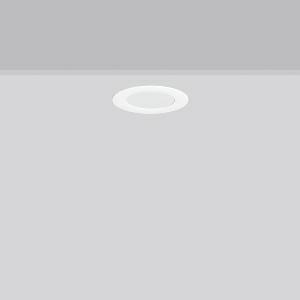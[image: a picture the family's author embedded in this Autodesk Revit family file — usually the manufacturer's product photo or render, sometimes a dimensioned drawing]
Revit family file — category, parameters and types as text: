
# Revit family: toledo_flat_round_e_672228_002_47f1
name_source: partatom
category: Lighting Fixtures
units: mm (PartAtom-declared; Revit-internal decimal feet)

## family parameters
Cut with Voids When Loaded = No
Host = Face
Light Source = No
Part Type = Normal
Room Calculation Point = No
Round Connector Dimension = Use Diameter
Shared = No

## types (1)
- TOLEDO FLAT round E (1 x LED Modul 830, 470 lm, 3000)
    Apparent Load = 5 VA
    CIE Flux Codes = 48 79 96 100 100
    Color Rendering = 80
    Color Temperature = 3000
    Default Elevation = 1800 mm
    Description = Series: TOLEDO FLAT round
Ultra thin recessed downlight. For escape route illumination. Housing: die-cast aluminium, powder-coated. Lightguide and diffuser made of non-yellowing plastic (PMMA). Diffuser opal matt plastic. Ceiling installation with spring system. Including separate LED converter with connecting cable 250 mm. Suitable for connection to central battery systems. External driver with simple plug-in locking system. 
Colour: white
Diameter: 148 mm
Height: 2 mm
Cut-out diameter: 128 mm
Recess height: 35 mm
Luminaire: recess height: 31-51 mm
Weight: 293 g
Operating mode: maintained power mode
Lamp: LED
Socket: without socket
Colour temperature: 3000K
Colour rendering index (CRI): 80
System power: 5 W
Rated luminous flux: 470 lm
Luminous flux, emergency: 470 lm
System power, emergency: 5 W
Control gear: Regulated power supply
Protection class: II
Type of protection: IP 54
    Height = 0 mm  [stored 0 ft]
    Lamp = 1 x LED Modul 830
    Lamp Light Flux = 470 lm
    Lamp count = 1
    Length = 148 mm
    Lifetime = 50000 h
    Luminous efficacy = 94 lm/W
    Manufacturer = RZB
    ModVariant = No
    Model = 672228.002
    Mounting Place = Ceiling
    Mounting Type = Recessed
    Number of Poles = 1
    OnlyDefault = Yes
    Power Factor = 1
    Product Name = TOLEDO FLAT round E
    Product group = Recessed downlights
    ProductGroupID = 402
    Protection Class = Protection class II
    Protection Degree = IP 40
    RLX_Detail_Level = 1
    RLX_Emergency_Light_Flux = 470 lm
    RLX_Emergency_Type = 3
    RLX_Emergency_Type_DB = Yes
    RlxData = <blob elided: 27333 chars, md5=b5129532>
    Socket = socket
    Standby Power = 0 W
    System Light Flux = 470 lm
    System Power = 5 W
    Type Comments = Product without accessories
    Type Image = 901451.002.jpg
    URL = http://relux.com
    VarID = ---
    Voltage = 230 V
    Voltage Range = 220-240 V
    Weight = 0.00 kg
    Width = 0 mm  [stored 0 ft]

note: [stored X ft] marks values corroborated as IEEE doubles in the binary element streams (Revit-internal decimal feet)

## geometry (parser evidence)
native form markers: Blend x4, Sweep x12
no freeform markers — native parametric forms only
